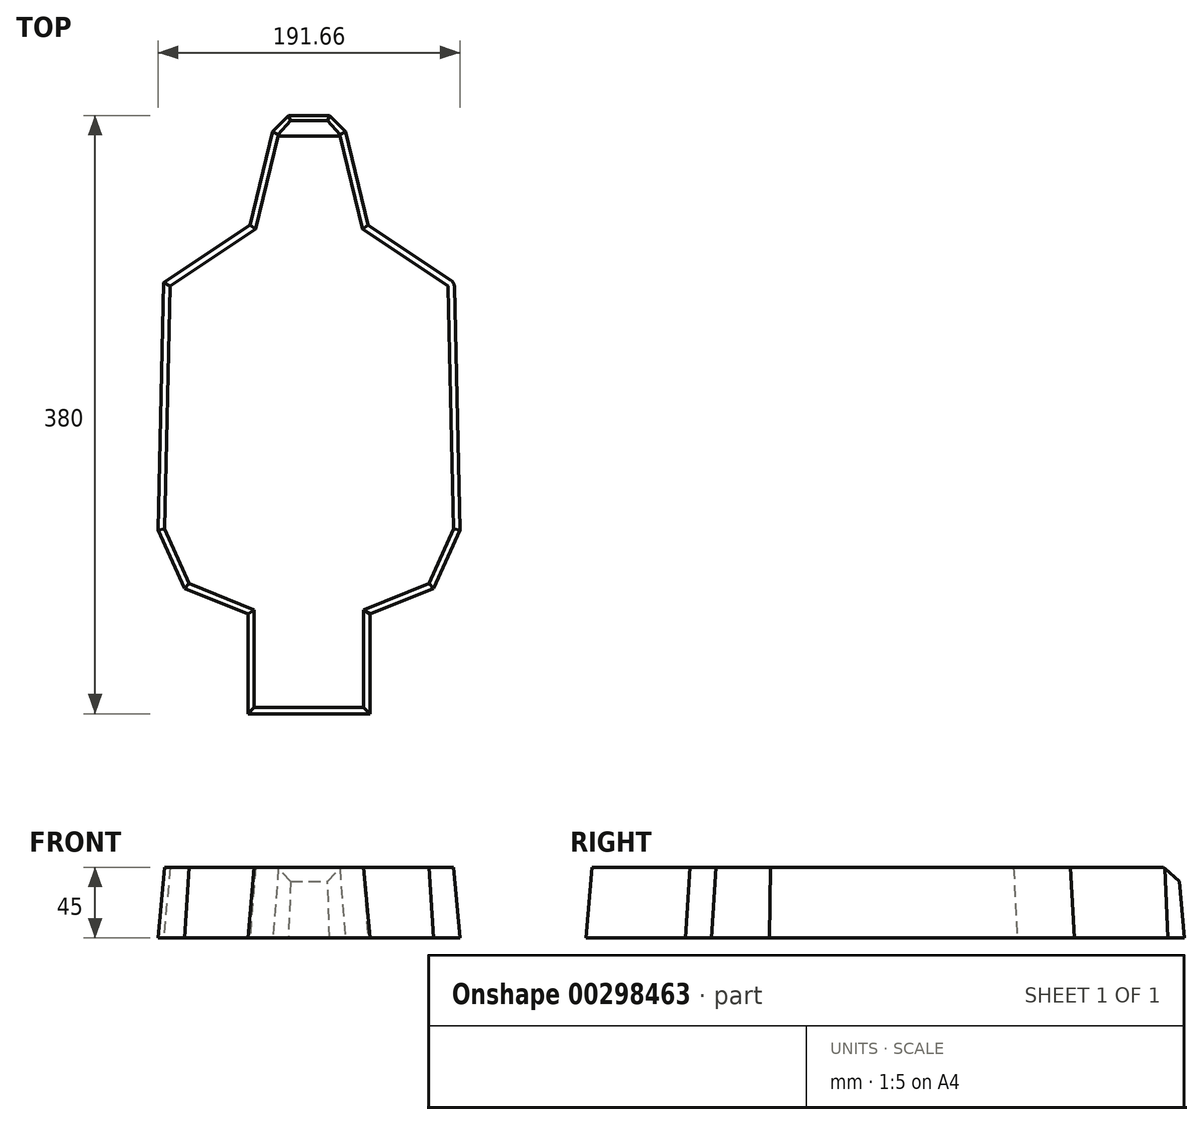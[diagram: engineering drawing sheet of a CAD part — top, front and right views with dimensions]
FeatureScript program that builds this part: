
annotation { "Feature Type Name" : "Feature", "Feature Type Description" : "" }
export const myFeature = defineFeature(function(context is Context, id is Id, definition is map)
    precondition{}
    {
        {
            var Q0;
            Q0=qCreatedBy(makeId("Top.planeOp"),FACE);
            var sketch = newSketch(context, id + "F0", { "sketchPlane" : qUnion([Q0])});
            skLineSegment(sketch, "E0", {"start": v(0, -190) * mm, "end": v(0, 190) * mm, "construction": true});
            skLineSegment(sketch, "E1", {"start": v(0, -190) * mm, "end": v(-38.7, -190) * mm});
            skLineSegment(sketch, "E2", {"start": v(-38.7, -190) * mm, "end": v(-38.7, -126.7) * mm});
            skLineSegment(sketch, "E3", {"start": v(-38.7, -126.7) * mm, "end": v(-79.16, -110.37) * mm});
            skLineSegment(sketch, "E4", {"start": v(-79.16, -110.37) * mm, "end": v(-95.83, -73.42) * mm});
            skLineSegment(sketch, "E5", {"start": v(-95.83, -73.42) * mm, "end": v(-92.26, 83.79) * mm});
            skLineSegment(sketch, "E6", {"start": v(-92.26, 83.79) * mm, "end": v(-37.5, 120.3) * mm});
            skLineSegment(sketch, "E7", {"start": v(0, 190) * mm, "end": v(-13.1, 190) * mm});
            skLineSegment(sketch, "E8.MirrorCS", {"start": v(0, 190) * mm, "end": v(13.1, 190) * mm});
            skLineSegment(sketch, "E9.MirrorCS", {"start": v(90.1, 85.23) * mm, "end": v(37.5, 120.3) * mm});
            skLineSegment(sketch, "E10.MirrorCS", {"start": v(95.83, -73.42) * mm, "end": v(92.32, 81.19) * mm});
            skLineSegment(sketch, "E11.MirrorCS", {"start": v(79.16, -110.37) * mm, "end": v(95.83, -73.42) * mm});
            skLineSegment(sketch, "E12.MirrorCS", {"start": v(38.7, -126.7) * mm, "end": v(79.16, -110.37) * mm});
            skLineSegment(sketch, "E13.MirrorCS", {"start": v(38.7, -190) * mm, "end": v(38.7, -126.7) * mm});
            skLineSegment(sketch, "E14.MirrorCS", {"start": v(0, -190) * mm, "end": v(38.7, -190) * mm});
            skLineSegment(sketch, "E15", {"start": v(-37.5, 120.3) * mm, "end": v(-23.05, 179.62) * mm});
            skLineSegment(sketch, "E16", {"start": v(-23.05, 179.62) * mm, "end": v(-13.1, 190) * mm});
            skLineSegment(sketch, "E17.MirrorCS", {"start": v(23.05, 179.62) * mm, "end": v(13.1, 190) * mm});
            skLineSegment(sketch, "E18.MirrorCS", {"start": v(37.5, 120.3) * mm, "end": v(23.05, 179.62) * mm});
            skLineSegment(sketch, "E19", {"start": v(-95.83, -73.42) * mm, "end": v(95.83, -73.42) * mm, "construction": true});
            skLineSegment(sketch, "E20", {"start": v(-38.7, -126.7) * mm, "end": v(-37.5, 120.3) * mm, "construction": true});
            skLineSegment(sketch, "E21", {"start": v(38.7, -126.7) * mm, "end": v(37.5, 120.3) * mm, "construction": true});
            skLineSegment(sketch, "E22", {"start": v(-37.5, 120.3) * mm, "end": v(37.5, 120.3) * mm, "construction": true});
            skLineSegment(sketch, "E23", {"start": v(-92.26, 83.79) * mm, "end": v(92.26, 83.79) * mm, "construction": true});
            skPoint(sketch, "E24", {"position": v(0, 83.79) * mm});
            skPoint(sketch, "E25", {"position": v(0, 91.77) * mm});
            skPoint(sketch, "E26", {"position": v(0, -73.42) * mm});
            skLineSegment(sketch, "E27", {"start": v(-38.7, -150.38) * mm, "end": v(38.7, -150.38) * mm, "construction": true});
            skPoint(sketch, "E28.visualSharp", {"position": v(92.26, 83.79) * mm});
            skArc(sketch, "E28.filletArc", {"start": v(92.32, 81.19) * mm, "mid": v(91.7, 83.48) * mm, "end": v(90.1, 85.23) * mm});
            skSolve(sketch);
        }
        {
            var Q0;
            Q0=qCreatedBy(makeId("Right.planeOp"),FACE);
            var sketch = newSketch(context, id + "F1", { "sketchPlane" : qUnion([Q0])});
            skSolve(sketch);
        }
        {
            var Q0;
            Q0 = qSketchRegion(id + "F0", true);
            extrude(context, id + "F2", {"entities" : qUnion([Q0]), "depth" : 45 * mm, "hasDraft" : true, "draftAngle" : 5 * degree, "draftPullDirection" : true});
        }
        {
            var Q0;
            Q0=makeQuery(id+"F2.opExtrude","CAP_FACE",FACE,{"disambiguationData":[OSD([sQuery(id+"F0.wireOp",EDGE,"E1"),sQuery(id+"F0.wireOp",EDGE,"E2"),sQuery(id+"F0.wireOp",EDGE,"E3"),sQuery(id+"F0.wireOp",EDGE,"E4"),sQuery(id+"F0.wireOp",EDGE,"E5"),sQuery(id+"F0.wireOp",EDGE,"E6"),sQuery(id+"F0.wireOp",EDGE,"E7"),sQuery(id+"F0.wireOp",EDGE,"E8.MirrorCS"),sQuery(id+"F0.wireOp",EDGE,"E9.MirrorCS"),sQuery(id+"F0.wireOp",EDGE,"E10.MirrorCS"),sQuery(id+"F0.wireOp",EDGE,"E11.MirrorCS"),sQuery(id+"F0.wireOp",EDGE,"E12.MirrorCS"),sQuery(id+"F0.wireOp",EDGE,"E13.MirrorCS"),sQuery(id+"F0.wireOp",EDGE,"E14.MirrorCS"),sQuery(id+"F0.wireOp",EDGE,"E15"),sQuery(id+"F0.wireOp",EDGE,"E16"),sQuery(id+"F0.wireOp",EDGE,"E17.MirrorCS"),sQuery(id+"F0.wireOp",EDGE,"E18.MirrorCS")])],"isStart":false});
            var sketch = newSketch(context, id + "F3", { "sketchPlane" : qUnion([Q0])});
            skLineSegment(sketch, "E29", {"start": v(-19.48, 177.66) * mm, "end": v(19.48, 177.66) * mm, "construction": true});
            skLineSegment(sketch, "E30", {"start": v(-34.04, 117.87) * mm, "end": v(34.04, 117.87) * mm, "construction": true});
            skLineSegment(sketch, "E31", {"start": v(34.04, 117.87) * mm, "end": v(34.76, -124.05) * mm, "construction": true});
            skLineSegment(sketch, "E32", {"start": v(-34.76, -124.05) * mm, "end": v(-34.04, 117.87) * mm, "construction": true});
            skLineSegment(sketch, "E33", {"start": v(-34.76, -124.05) * mm, "end": v(34.76, -124.05) * mm, "construction": true});
            skLineSegment(sketch, "E34", {"start": v(-34.76, -124.05) * mm, "end": v(-34.76, -186.06) * mm, "construction": true});
            skLineSegment(sketch, "E35", {"start": v(-34.76, -186.06) * mm, "end": v(34.76, -186.06) * mm, "construction": true});
            skLineSegment(sketch, "E36", {"start": v(34.76, -186.06) * mm, "end": v(34.76, -124.05) * mm, "construction": true});
            skLineSegment(sketch, "E37", {"start": v(-34.04, 117.87) * mm, "end": v(-19.48, 177.66) * mm, "construction": true});
            skLineSegment(sketch, "E38", {"start": v(-11.42, 186.06) * mm, "end": v(-19.48, 177.66) * mm, "construction": true});
            skLineSegment(sketch, "E39", {"start": v(-11.42, 186.06) * mm, "end": v(11.42, 186.06) * mm, "construction": true});
            skLineSegment(sketch, "E40", {"start": v(11.42, 186.06) * mm, "end": v(19.48, 177.66) * mm, "construction": true});
            skLineSegment(sketch, "E41", {"start": v(34.04, 117.87) * mm, "end": v(19.48, 177.66) * mm, "construction": true});
            skSolve(sketch);
        }
        {
            var Q0;
            Q0=makeQuery(id+"F2.opExtrude","CAP_EDGE",EDGE,{"disambiguationData":[OSD([sQuery(id+"F0.wireOp",EDGE,"E7"),sQuery(id+"F0.wireOp",EDGE,"E8.MirrorCS")])],"isStart":false});
            chamfer(context, id + "F4", {"entities" : qUnion([Q0]), "width" : 10 * mm, "tangentPropagation" : true});
        }
    });
